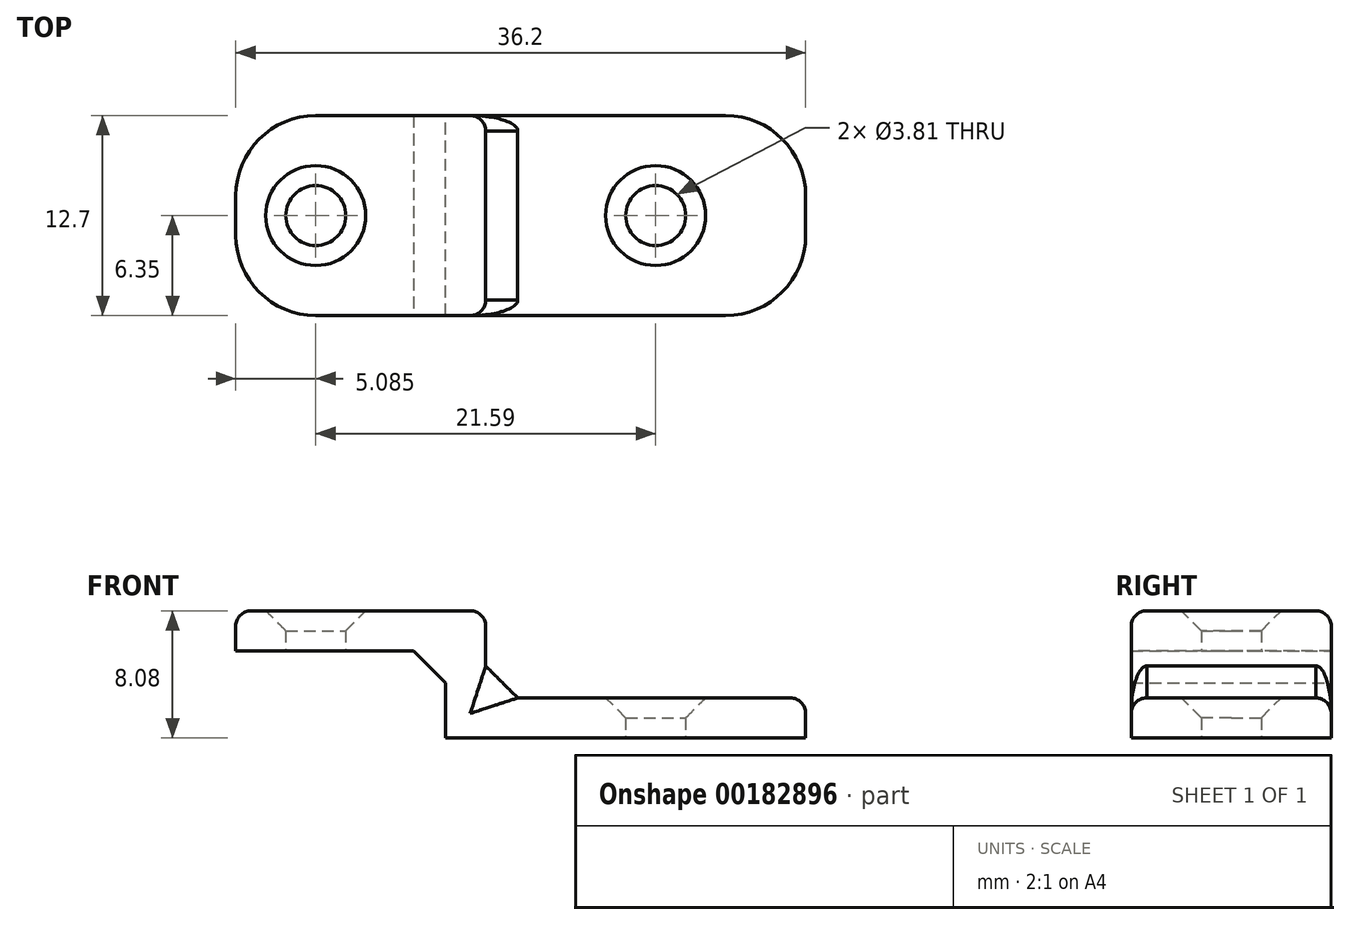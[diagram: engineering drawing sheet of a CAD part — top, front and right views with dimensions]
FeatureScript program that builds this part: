
annotation { "Feature Type Name" : "Feature", "Feature Type Description" : "" }
export const myFeature = defineFeature(function(context is Context, id is Id, definition is map)
    precondition{}
    {
        {
            var Q0;
            Q0=qCreatedBy(makeId("Front.planeOp"),FACE);
            var sketch = newSketch(context, id + "F0", { "sketchPlane" : qUnion([Q0])});
            skLineSegment(sketch, "E0", {"start": v(0, 0) * mm, "end": v(0, 1.5) * mm});
            skLineSegment(sketch, "E1", {"start": v(0, 1.5) * mm, "end": v(-13.33, 1.5) * mm});
            skLineSegment(sketch, "E2.0", {"start": v(2.54, 4.04) * mm, "end": v(-13.33, 4.04) * mm});
            skLineSegment(sketch, "E2.1", {"start": v(2.54, 0) * mm, "end": v(2.54, 4.04) * mm});
            skLineSegment(sketch, "E3", {"start": v(-13.33, 4.04) * mm, "end": v(-13.33, 1.5) * mm});
            skLineSegment(sketch, "E4", {"start": v(0, 3.3) * mm, "end": v(0, -26.78) * mm, "construction": true});
            skLineSegment(sketch, "E5", {"start": v(-31.43, 0) * mm, "end": v(38.23, 0) * mm, "construction": true});
            skLineSegment(sketch, "E6.MirrorCS", {"start": v(2.54, -4.04) * mm, "end": v(0, -4.04) * mm});
            skLineSegment(sketch, "E7.MirrorCS", {"start": v(0, 0) * mm, "end": v(0, -1.5) * mm});
            skLineSegment(sketch, "E8.MirrorCS", {"start": v(2.54, 0) * mm, "end": v(2.54, -1.5) * mm});
            skLineSegment(sketch, "E9.MirrorCS", {"start": v(22.86, -4.04) * mm, "end": v(22.86, -1.5) * mm});
            skLineSegment(sketch, "E10.MirrorCS", {"start": v(0, -4.04) * mm, "end": v(22.86, -4.04) * mm});
            skLineSegment(sketch, "E11.MirrorCS", {"start": v(2.54, -1.5) * mm, "end": v(22.86, -1.5) * mm});
            skLineSegment(sketch, "E12", {"start": v(0, -1.5) * mm, "end": v(0, -4.04) * mm});
            skSolve(sketch);
        }
        {
            var Q0;
            Q0 = qSketchRegion(id + "F0", true);
            extrude(context, id + "F1", {"entities" : qUnion([Q0]), "depth" : 12.7 * mm});
        }
        {
            var Q0;
            Q0=qCreatedBy(makeId("Top.planeOp"),FACE);
            var sketch = newSketch(context, id + "F2", { "sketchPlane" : qUnion([Q0])});
            skLineSegment(sketch, "E13.0", {"start": v(-13.33, -12.7) * mm, "end": v(-13.33, 0) * mm, "construction": true});
            skCircle(sketch, "E14", {"center": v(-8.25, -6.35) * mm, "radius": 1.9 * mm});
            skPoint(sketch, "E14.centerSnap0", {"position": v(-13.33, -6.35) * mm});
            skLineSegment(sketch, "E15", {"start": v(0, -3.36) * mm, "end": v(0, 17.5) * mm, "construction": true});
            skLineSegment(sketch, "E16.0", {"start": v(2.54, -12.7) * mm, "end": v(2.54, 0) * mm, "construction": true});
            skCircle(sketch, "E17.MirrorC", {"center": v(13.33, -6.35) * mm, "radius": 1.9 * mm});
            skSolve(sketch);
        }
        {
            var Q0;
            Q0 = qSketchRegion(id + "F2", true);
            extrude(context, id + "F3", {"entities" : qUnion([Q0]), "operationType" : NewBodyOperationType.REMOVE, "endBound" : BoundingType.THROUGH_ALL, "depth" : 25.4 * mm, "hasSecondDirection" : true, "secondDirectionBound" : SecondDirectionBoundingType.THROUGH_ALL, "secondDirectionOppositeDirection" : true, "secondDirectionDepth" : 25.4 * mm});
        }
        {
            var Q0;
            Q0=makeQuery(id+"F1.opExtrude","CAP_EDGE",EDGE,{"disambiguationData":[OSD([sQuery(id+"F0.wireOp",EDGE,"E3")])],"isStart":false});
            var Q1;
            Q1=makeQuery(id+"F1.opExtrude","CAP_EDGE",EDGE,{"disambiguationData":[OSD([sQuery(id+"F0.wireOp",EDGE,"E3")])],"isStart":true});
            var Q2;
            Q2=makeQuery(id+"F1.opExtrude","CAP_EDGE",EDGE,{"disambiguationData":[OSD([sQuery(id+"F0.wireOp",EDGE,"E9.MirrorCS")])],"isStart":false});
            var Q3;
            Q3=makeQuery(id+"F1.opExtrude","CAP_EDGE",EDGE,{"disambiguationData":[OSD([sQuery(id+"F0.wireOp",EDGE,"E9.MirrorCS")])],"isStart":true});
            fillet(context, id + "F4", {"entities" : qUnion([Q0, Q1, Q2, Q3]), "radius" : 5.08 * mm, "tangentPropagation" : true, "allowEdgeOverflow" : false});
        }
        {
            var Q0;
            Q0=makeQuery(id+"F1.opExtrude","CAP_EDGE",EDGE,{"disambiguationData":[OSD([sQuery(id+"F0.wireOp",EDGE,"E2.0")])],"isStart":false});
            var Q1;
            Q1=makeQuery(id+"F1.opExtrude","CAP_EDGE",EDGE,{"disambiguationData":[OSD([sQuery(id+"F0.wireOp",EDGE,"E2.1"),sQuery(id+"F0.wireOp",EDGE,"E8.MirrorCS")])],"isStart":false});
            var Q2;
            Q2=makeQuery(id+"F1.opExtrude","CAP_EDGE",EDGE,{"disambiguationData":[OSD([sQuery(id+"F0.wireOp",EDGE,"E2.1"),sQuery(id+"F0.wireOp",EDGE,"E8.MirrorCS")])],"isStart":true});
            var Q3;
            Q3=makeQuery(id+"F1.opExtrude","CAP_EDGE",EDGE,{"disambiguationData":[OSD([sQuery(id+"F0.wireOp",EDGE,"E11.MirrorCS")])],"isStart":false});
            var Q4;
            Q4=makeQuery(id+"F1.opExtrude","SWEPT_EDGE",EDGE,{"disambiguationData":[OSD([sQuery(id+"F0.wireOp",EDGE,"E2.0"),sQuery(id+"F0.wireOp",EDGE,"E2.1")])]});
            fillet(context, id + "F5", {"entities" : qUnion([Q0, Q1, Q2, Q3, Q4]), "radius" : 0.98 * mm, "tangentPropagation" : true, "allowEdgeOverflow" : false});
        }
        {
            var Q0;
            Q0=makeQuery(id+"F3.boolean.opBoolean","INTERSECT",EDGE,{"derivedFrom":[makeQuery(id+"F1.opExtrude","SWEPT_FACE",FACE,{"disambiguationData":[OSD([sQuery(id+"F0.wireOp",EDGE,"E2.0")])]}),makeQuery(id+"F3.opExtrude","SWEPT_FACE",FACE,{"disambiguationData":[OSD([sQuery(id+"F2.wireOp",EDGE,"E14")])]})]});
            var Q1;
            Q1=makeQuery(id+"F3.boolean.opBoolean","INTERSECT",EDGE,{"derivedFrom":[makeQuery(id+"F1.opExtrude","SWEPT_FACE",FACE,{"disambiguationData":[OSD([sQuery(id+"F0.wireOp",EDGE,"E11.MirrorCS")])]}),makeQuery(id+"F3.opExtrude","SWEPT_FACE",FACE,{"disambiguationData":[OSD([sQuery(id+"F2.wireOp",EDGE,"E17.MirrorC")])]})]});
            chamfer(context, id + "F6", {"entities" : qUnion([Q0, Q1]), "width" : 1.27 * mm, "tangentPropagation" : true});
        }
        {
            var Q0;
            Q0=makeQuery(id+"F1.opExtrude","SWEPT_EDGE",EDGE,{"disambiguationData":[OSD([sQuery(id+"F0.wireOp",EDGE,"E8.MirrorCS"),sQuery(id+"F0.wireOp",EDGE,"E11.MirrorCS")])]});
            var Q1;
            Q1=makeQuery(id+"F1.opExtrude","SWEPT_EDGE",EDGE,{"disambiguationData":[OSD([sQuery(id+"F0.wireOp",EDGE,"E0"),sQuery(id+"F0.wireOp",EDGE,"E1")])]});
            chamfer(context, id + "F7", {"entities" : qUnion([Q0, Q1]), "width" : 2.03 * mm, "tangentPropagation" : true});
        }
    });
